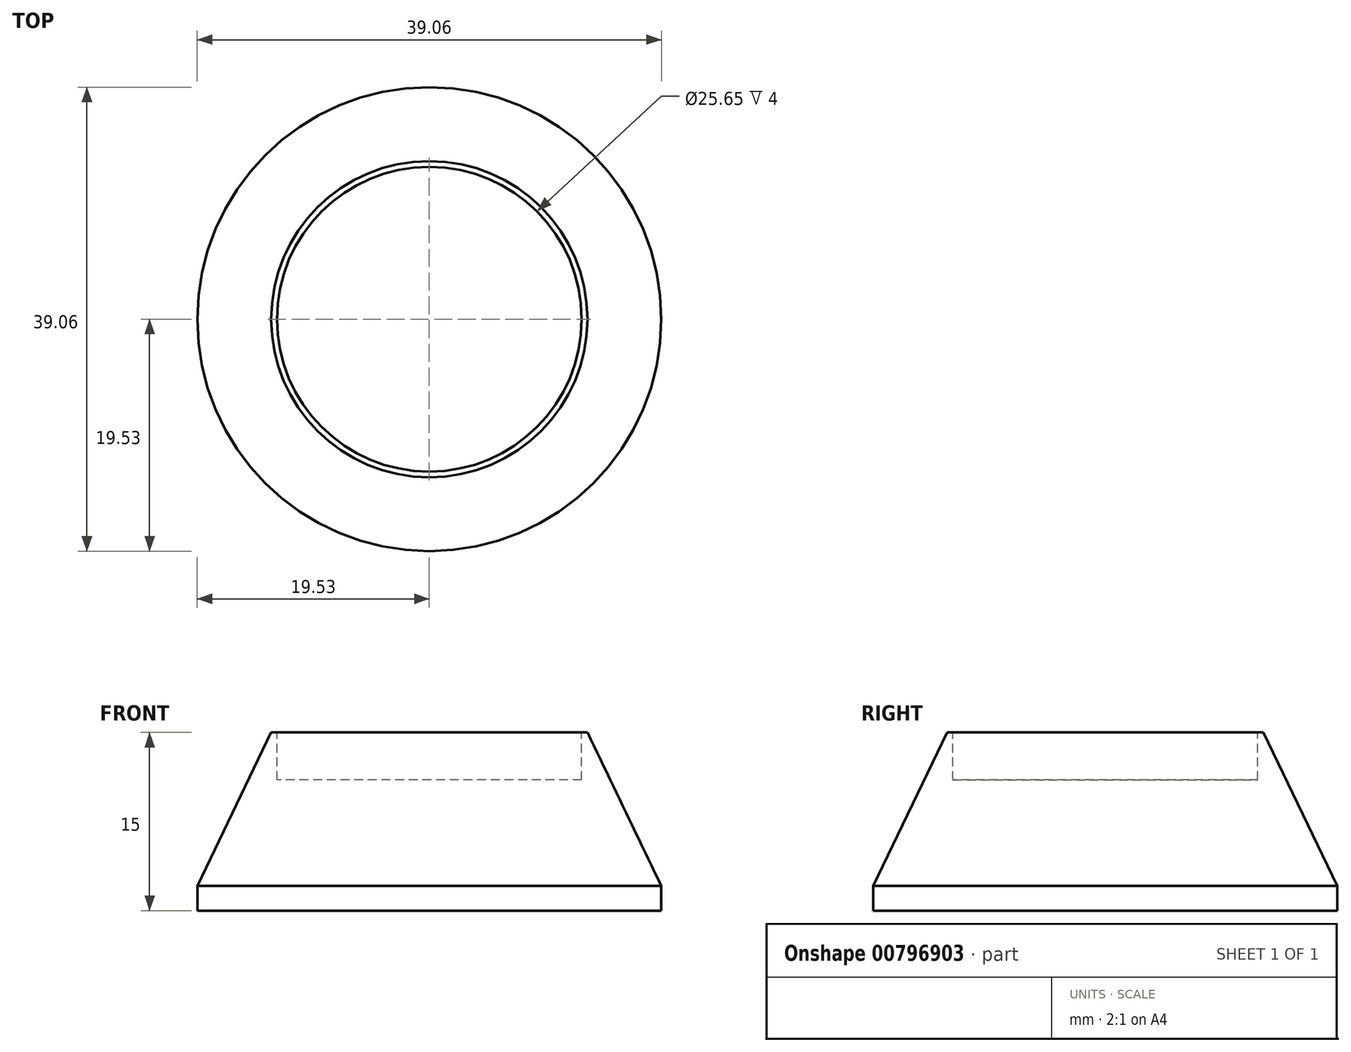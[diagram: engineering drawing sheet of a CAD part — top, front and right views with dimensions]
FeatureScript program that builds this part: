
annotation { "Feature Type Name" : "Feature", "Feature Type Description" : "" }
export const myFeature = defineFeature(function(context is Context, id is Id, definition is map)
    precondition{}
    {
        {
            var Q0;
            Q0=qCreatedBy(makeId("Front.planeOp"),FACE);
            var sketch = newSketch(context, id + "F0", { "sketchPlane" : qUnion([Q0])});
            skLineSegment(sketch, "E0", {"start": v(0, 0) * mm, "end": v(-12.82, 0) * mm});
            skLineSegment(sketch, "E1", {"start": v(-12.82, 0) * mm, "end": v(-12.82, 5) * mm});
            skLineSegment(sketch, "E2", {"start": v(-20.53, -11) * mm, "end": v(-12.82, 5) * mm});
            skLineSegment(sketch, "E3", {"start": v(-20.53, -11) * mm, "end": v(0, -11) * mm});
            skLineSegment(sketch, "E4", {"start": v(0, 0) * mm, "end": v(0, -11) * mm});
            skLineSegment(sketch, "E5", {"start": v(-12.82, 4) * mm, "end": v(-13.3, 4) * mm});
            skLineSegment(sketch, "E6", {"start": v(-19.53, -11) * mm, "end": v(-19.53, -8.92) * mm});
            skSolve(sketch);
        }
        {
            var Q0;
            Q0=makeQuery(id+"F0.imprint","IMPRINT",FACE,{"disambiguationData":[TD([[makeQuery(id+"F0.imprint","IMPRINT",EDGE,{"derivedFrom":sQuery(id+"F0.wireOp",EDGE,"E0")}),1.0]])]});
            var Q1;
            Q1=sQuery(id+"F0.wireOp",EDGE,"E4");
            revolve(context, id + "F1", {"surfaceOperationType" : NewSurfaceOperationType.NEW, "entities" : qUnion([Q0]), "axis" : qUnion([Q1]), "revolveType" : RevolveType.FULL});
        }
    });
